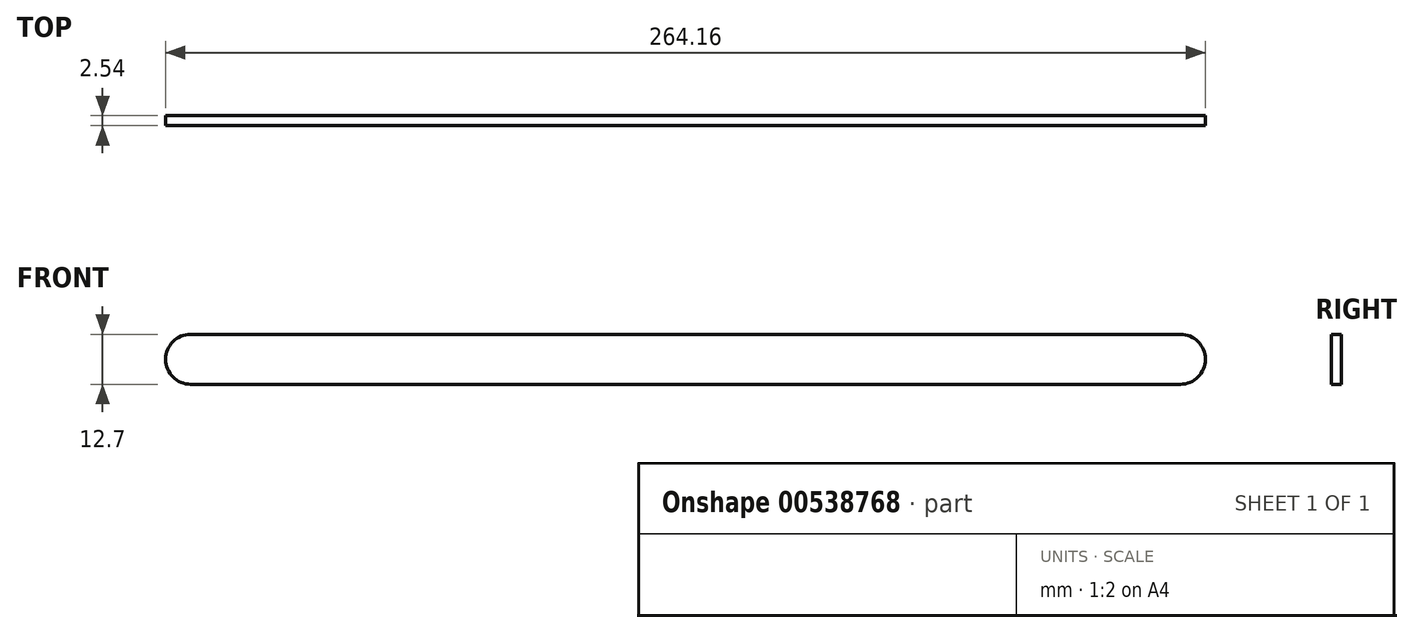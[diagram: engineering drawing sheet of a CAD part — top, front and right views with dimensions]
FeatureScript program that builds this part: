
annotation { "Feature Type Name" : "Feature", "Feature Type Description" : "" }
export const myFeature = defineFeature(function(context is Context, id is Id, definition is map)
    precondition{}
    {
        {
            var Q0;
            Q0=qCreatedBy(makeId("Front.planeOp"),FACE);
            var sketch = newSketch(context, id + "F0", { "sketchPlane" : qUnion([Q0])});
            skLineSegment(sketch, "E0", {"start": v(-125.73, 0) * mm, "end": v(125.73, 0) * mm});
            skLineSegment(sketch, "E1", {"start": v(-125.73, 6.35) * mm, "end": v(125.73, 6.35) * mm});
            skLineSegment(sketch, "E2", {"start": v(-125.73, -6.35) * mm, "end": v(125.73, -6.35) * mm});
            skArc(sketch, "E3", {"start": v(-125.73, 6.35) * mm, "mid": v(-132.08, 0) * mm, "end": v(-125.73, -6.35) * mm});
            skArc(sketch, "E4", {"start": v(125.73, 6.35) * mm, "mid": v(132.08, 0) * mm, "end": v(125.73, -6.35) * mm});
            skSolve(sketch);
        }
        {
            var Q0;
            Q0=qSketchRegion(id+"F0",true);
            extrude(context, id + "F1", {"entities" : qUnion([Q0]), "endBound" : BoundingType.SYMMETRIC, "depth" : 2.54 * mm, "offsetDistance" : 25.4 * mm});
        }
    });
